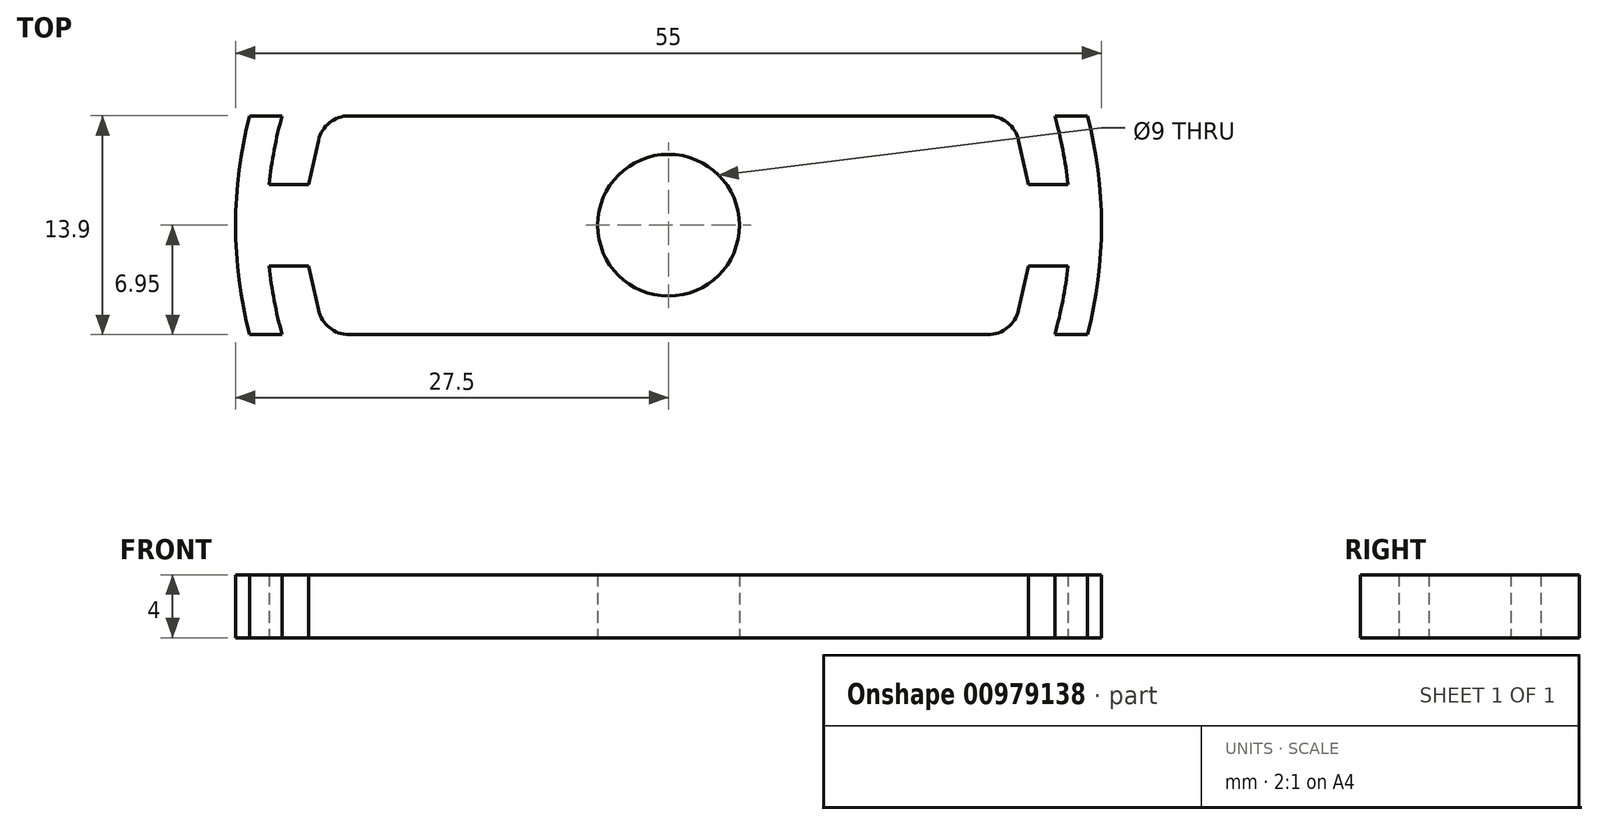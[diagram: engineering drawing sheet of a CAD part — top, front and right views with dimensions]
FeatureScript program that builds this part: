
annotation { "Feature Type Name" : "Feature", "Feature Type Description" : "" }
export const myFeature = defineFeature(function(context is Context, id is Id, definition is map)
    precondition{}
    {
        {
            var Q0;
            Q0=qCreatedBy(makeId("Top.planeOp"),FACE);
            var sketch = newSketch(context, id + "F0", { "sketchPlane" : qUnion([Q0])});
            skCircle(sketch, "E0", {"center": v(0, 0) * mm, "radius": 25.5 * mm});
            skCircle(sketch, "E1", {"center": v(0, 0) * mm, "radius": 27.5 * mm});
            skCircle(sketch, "E2", {"center": v(0, 0) * mm, "radius": 4.5 * mm});
            skLineSegment(sketch, "E3", {"start": v(-25.37, 2.6) * mm, "end": v(-22.87, 2.6) * mm});
            skLineSegment(sketch, "E4", {"start": v(-22.87, 2.6) * mm, "end": v(-21.88, 6.95) * mm});
            skLineSegment(sketch, "E5", {"start": v(-21.88, 6.95) * mm, "end": v(0, 6.95) * mm});
            skLineSegment(sketch, "E6.MirrorCS", {"start": v(-25.37, -2.6) * mm, "end": v(-22.87, -2.6) * mm});
            skLineSegment(sketch, "E7.MirrorCS", {"start": v(-21.88, -6.95) * mm, "end": v(0, -6.95) * mm});
            skLineSegment(sketch, "E8.MirrorCS", {"start": v(-22.87, -2.6) * mm, "end": v(-21.88, -6.95) * mm});
            skLineSegment(sketch, "E9.MirrorCS", {"start": v(-22.87, 2.6) * mm, "end": v(-22.23, 5.39) * mm});
            skLineSegment(sketch, "E10.MirrorCS", {"start": v(-22.87, -2.6) * mm, "end": v(-22.23, -5.39) * mm});
            skLineSegment(sketch, "E11.MirrorCS", {"start": v(-20.28, 6.95) * mm, "end": v(0, 6.95) * mm});
            skLineSegment(sketch, "E12.MirrorCS", {"start": v(-20.28, -6.95) * mm, "end": v(0, -6.95) * mm});
            skLineSegment(sketch, "E13.MirrorCS", {"start": v(22.87, -2.6) * mm, "end": v(22.23, -5.39) * mm});
            skLineSegment(sketch, "E14.MirrorCS", {"start": v(20.28, -6.95) * mm, "end": v(0, -6.95) * mm});
            skLineSegment(sketch, "E15.MirrorCS", {"start": v(25.37, -2.6) * mm, "end": v(22.87, -2.6) * mm});
            skLineSegment(sketch, "E16.MirrorCS", {"start": v(22.87, 2.6) * mm, "end": v(21.88, 6.95) * mm});
            skLineSegment(sketch, "E17.MirrorCS", {"start": v(20.28, 6.95) * mm, "end": v(0, 6.95) * mm});
            skLineSegment(sketch, "E18.MirrorCS", {"start": v(25.37, 2.6) * mm, "end": v(22.87, 2.6) * mm});
            skLineSegment(sketch, "E19.MirrorCS", {"start": v(22.87, 2.6) * mm, "end": v(22.23, 5.39) * mm});
            skLineSegment(sketch, "E20.MirrorCS", {"start": v(22.87, -2.6) * mm, "end": v(21.88, -6.95) * mm});
            skLineSegment(sketch, "E21.MirrorCS", {"start": v(21.88, 6.95) * mm, "end": v(0, 6.95) * mm});
            skLineSegment(sketch, "E22.MirrorCS", {"start": v(21.88, -6.95) * mm, "end": v(0, -6.95) * mm});
            skLineSegment(sketch, "E23", {"start": v(-24.54, 6.95) * mm, "end": v(-26.6, 6.95) * mm});
            skLineSegment(sketch, "E24", {"start": v(-24.54, -6.95) * mm, "end": v(-26.6, -6.95) * mm});
            skLineSegment(sketch, "E25", {"start": v(24.54, 6.95) * mm, "end": v(26.6, 6.95) * mm});
            skLineSegment(sketch, "E26", {"start": v(24.54, -6.95) * mm, "end": v(26.6, -6.95) * mm});
            skPoint(sketch, "E27.visualSharp", {"position": v(-21.88, 6.95) * mm});
            skArc(sketch, "E27.filletArc", {"start": v(-20.28, 6.95) * mm, "mid": v(-21.53, 6.5) * mm, "end": v(-22.23, 5.39) * mm});
            skPoint(sketch, "E28.visualSharp", {"position": v(21.88, 6.95) * mm});
            skArc(sketch, "E28.filletArc", {"start": v(22.23, 5.39) * mm, "mid": v(21.53, 6.5) * mm, "end": v(20.28, 6.95) * mm});
            skPoint(sketch, "E29.visualSharp", {"position": v(21.88, -6.95) * mm});
            skArc(sketch, "E29.filletArc", {"start": v(20.28, -6.95) * mm, "mid": v(21.53, -6.5) * mm, "end": v(22.23, -5.39) * mm});
            skPoint(sketch, "E30.visualSharp", {"position": v(-21.88, -6.95) * mm});
            skArc(sketch, "E30.filletArc", {"start": v(-22.23, -5.39) * mm, "mid": v(-21.53, -6.5) * mm, "end": v(-20.28, -6.95) * mm});
            skSolve(sketch);
        }
        {
            var Q0;
            {var subQ0=sQuery(id+"F0.wireOp",EDGE,"E23");Q0=makeQuery(id+"F0.imprint","IMPRINT",FACE,{"disambiguationData":[TD([[makeQuery(id+"F0.imprint","IMPRINT",EDGE,{"derivedFrom":subQ0}),1.0]])]});}
            var Q1;
            {var subQ3=sQuery(id+"F0.wireOp",EDGE,"E25");Q1=makeQuery(id+"F0.imprint","IMPRINT",FACE,{"disambiguationData":[TD([[makeQuery(id+"F0.imprint","IMPRINT",EDGE,{"derivedFrom":subQ3}),-1.0]])]});}
            var Q2;
            Q2=makeQuery(id+"F0.imprint","IMPRINT",FACE,{"disambiguationData":[TD([[makeQuery(id+"F0.imprint","IMPRINT",EDGE,{"derivedFrom":sQuery(id+"F0.wireOp",EDGE,"E2")}),-1.0]])]});
            extrude(context, id + "F1", {"entities" : qUnion([Q0, Q1, Q2]), "depth" : 4 * mm, "offsetDistance" : 25 * mm});
        }
    });
